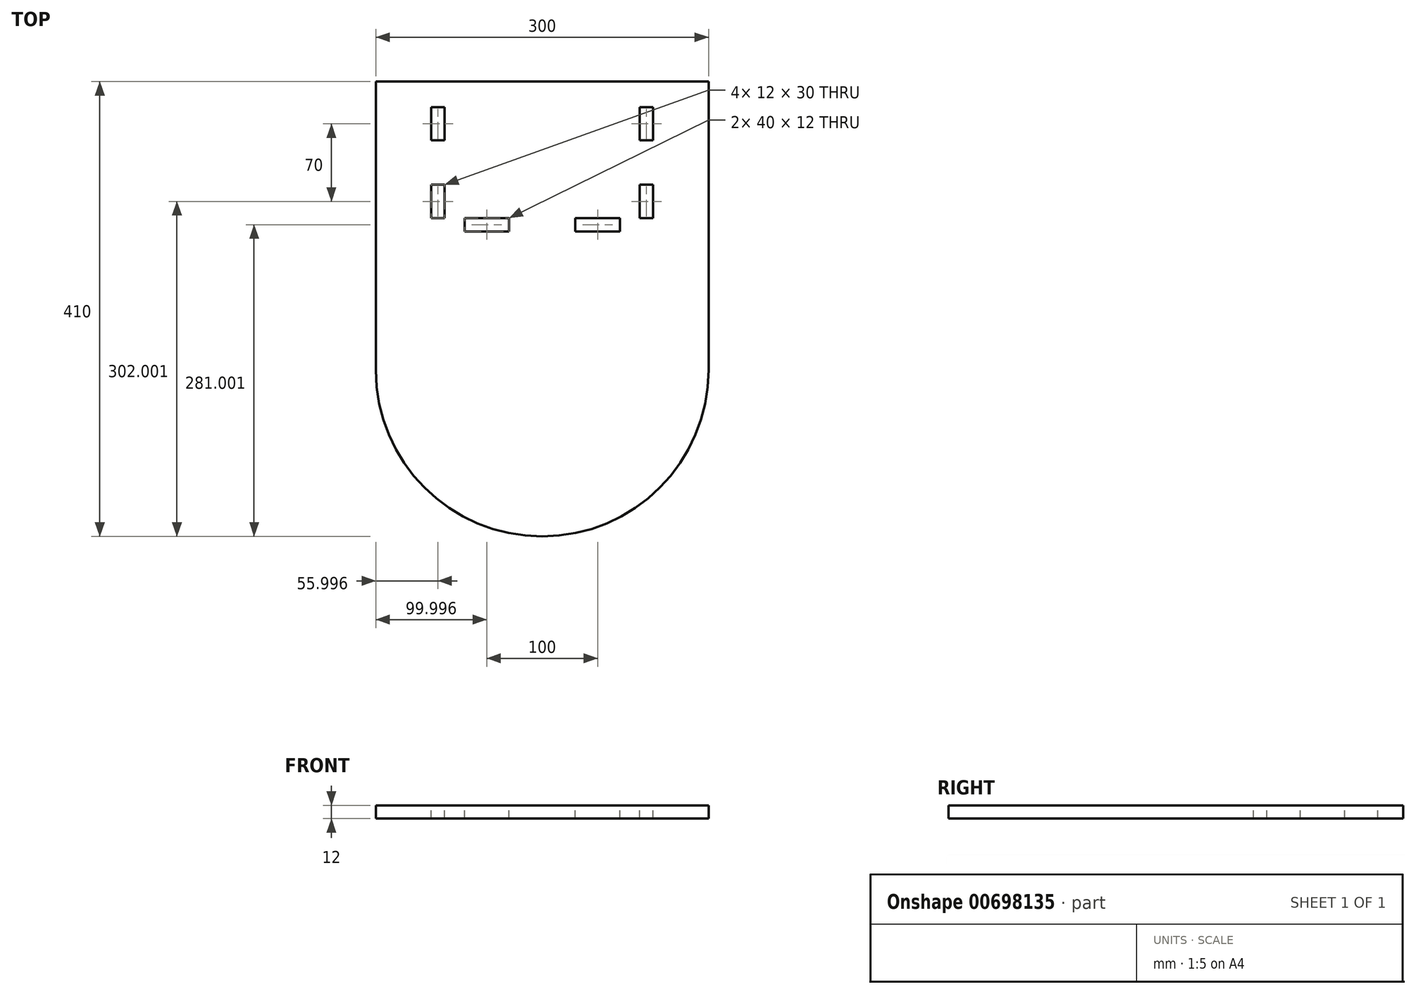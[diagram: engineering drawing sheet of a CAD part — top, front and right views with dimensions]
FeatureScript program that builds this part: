
annotation { "Feature Type Name" : "Feature", "Feature Type Description" : "" }
export const myFeature = defineFeature(function(context is Context, id is Id, definition is map)
    precondition{}
    {
        {
            assignVariable(context, id + "F0", {"name" : "wood", "anyValue" : 12 * mm});
        }
        {
            var Q0;
            Q0=qCreatedBy(makeId("Top.planeOp"),FACE);
            var sketch = newSketch(context, id + "F1", { "sketchPlane" : qUnion([Q0])});
            skCircle(sketch, "E0", {"center": v(-10.57, -1.95) * mm, "radius": 150 * mm});
            skLineSegment(sketch, "E1.bottom", {"start": v(-160.57, -1.95) * mm, "end": v(139.43, -1.95) * mm});
            skLineSegment(sketch, "E1.top", {"start": v(-160.57, 258.05) * mm, "end": v(139.43, 258.05) * mm});
            skLineSegment(sketch, "E1.left", {"start": v(-160.57, -1.95) * mm, "end": v(-160.57, 258.05) * mm});
            skLineSegment(sketch, "E1.right", {"start": v(139.43, -1.95) * mm, "end": v(139.43, 258.05) * mm});
            skCircle(sketch, "E2", {"center": v(-10.57, -1.95) * mm, "radius": 100 * mm, "construction": true});
            skSolve(sketch);
        }
        {
            var Q0;
            Q0=makeQuery(id+"F1.imprint","IMPRINT",FACE,{"disambiguationData":[TD([[makeQuery(id+"F1.imprint","IMPRINT",EDGE,{"derivedFrom":sQuery(id+"F1.wireOp",EDGE,"E1.top")}),-1.0]])]});
            var Q1;
            {var subQ0=sQuery(id+"F1.wireOp",EDGE,"E1.bottom");Q1=makeQuery(id+"F1.imprint","IMPRINT",FACE,{"disambiguationData":[TD([[makeQuery(id+"F1.imprint","IMPRINT",EDGE,{"derivedFrom":subQ0}),-1.0]])]});}
            var Q2;
            {var subQ0=sQuery(id+"F1.wireOp",EDGE,"E1.bottom");Q2=makeQuery(id+"F1.imprint","IMPRINT",FACE,{"disambiguationData":[TD([[makeQuery(id+"F1.imprint","IMPRINT",EDGE,{"derivedFrom":subQ0}),1.0]])]});}
            extrude(context, id + "F2", {"entities" : qUnion([Q0, Q1, Q2]), "depth" : getVariable(context, 'wood'), "offsetDistance" : 25 * mm});
        }
        {
            var Q0;
            Q0=makeQuery(id+"F2.opExtrude","CAP_FACE",FACE,{"disambiguationData":[OSD([sQuery(id+"F1.wireOp",EDGE,"E0"),sQuery(id+"F1.wireOp",EDGE,"E1.top"),sQuery(id+"F1.wireOp",EDGE,"E1.left"),sQuery(id+"F1.wireOp",EDGE,"E1.right")])],"isStart":false});
            var sketch = newSketch(context, id + "F3", { "sketchPlane" : qUnion([Q0])});
            skLineSegment(sketch, "E3", {"start": v(-10.57, 276.61) * mm, "end": v(-10.57, -30.99) * mm, "construction": true});
            skPoint(sketch, "E3.startSnap0", {"position": v(-10.57, 258.05) * mm});
            skLineSegment(sketch, "E4.bottom", {"start": v(-110.57, 165.05) * mm, "end": v(-98.57, 165.05) * mm});
            skLineSegment(sketch, "E4.top", {"start": v(-110.57, 135.05) * mm, "end": v(-98.57, 135.05) * mm});
            skLineSegment(sketch, "E4.left", {"start": v(-110.57, 165.05) * mm, "end": v(-110.57, 135.05) * mm});
            skLineSegment(sketch, "E4.right", {"start": v(-98.57, 165.05) * mm, "end": v(-98.57, 135.05) * mm});
            skLineSegment(sketch, "E5.bottom", {"start": v(-110.57, 235.05) * mm, "end": v(-98.57, 235.05) * mm});
            skLineSegment(sketch, "E5.top", {"start": v(-110.57, 205.05) * mm, "end": v(-98.57, 205.05) * mm});
            skLineSegment(sketch, "E5.left", {"start": v(-110.57, 235.05) * mm, "end": v(-110.57, 205.05) * mm});
            skLineSegment(sketch, "E5.right", {"start": v(-98.57, 235.05) * mm, "end": v(-98.57, 205.05) * mm});
            skLineSegment(sketch, "E6.bottom", {"start": v(-80.57, 135.05) * mm, "end": v(-40.57, 135.05) * mm});
            skLineSegment(sketch, "E6.top", {"start": v(-80.57, 123.05) * mm, "end": v(-40.57, 123.05) * mm});
            skLineSegment(sketch, "E6.left", {"start": v(-80.57, 135.05) * mm, "end": v(-80.57, 123.05) * mm});
            skLineSegment(sketch, "E6.right", {"start": v(-40.57, 135.05) * mm, "end": v(-40.57, 123.05) * mm});
            skLineSegment(sketch, "E7.MirrorCS", {"start": v(77.43, 235.05) * mm, "end": v(77.43, 205.05) * mm});
            skLineSegment(sketch, "E8.MirrorCS", {"start": v(19.43, 135.05) * mm, "end": v(19.43, 123.05) * mm});
            skLineSegment(sketch, "E9.MirrorCS", {"start": v(59.43, 135.05) * mm, "end": v(59.43, 123.05) * mm});
            skLineSegment(sketch, "E10.MirrorCS", {"start": v(59.43, 135.05) * mm, "end": v(19.43, 135.05) * mm});
            skLineSegment(sketch, "E11.MirrorCS", {"start": v(89.43, 235.05) * mm, "end": v(77.43, 235.05) * mm});
            skLineSegment(sketch, "E12.MirrorCS", {"start": v(59.43, 123.05) * mm, "end": v(19.43, 123.05) * mm});
            skLineSegment(sketch, "E13.MirrorCS", {"start": v(89.43, 165.05) * mm, "end": v(77.43, 165.05) * mm});
            skLineSegment(sketch, "E14.MirrorCS", {"start": v(89.43, 135.05) * mm, "end": v(77.43, 135.05) * mm});
            skLineSegment(sketch, "E15.MirrorCS", {"start": v(89.43, 205.05) * mm, "end": v(77.43, 205.05) * mm});
            skLineSegment(sketch, "E16.MirrorCS", {"start": v(89.43, 165.05) * mm, "end": v(89.43, 135.05) * mm});
            skLineSegment(sketch, "E17.MirrorCS", {"start": v(89.43, 235.05) * mm, "end": v(89.43, 205.05) * mm});
            skLineSegment(sketch, "E18.MirrorCS", {"start": v(77.43, 165.05) * mm, "end": v(77.43, 135.05) * mm});
            skSolve(sketch);
        }
        {
            var Q0;
            Q0 = qSketchRegion(id + "F3", true);
            extrude(context, id + "F4", {"entities" : qUnion([Q0]), "operationType" : NewBodyOperationType.REMOVE, "endBound" : BoundingType.UP_TO_NEXT, "oppositeDirection" : true, "depth" : 25 * mm, "offsetDistance" : 25 * mm});
        }
    });
